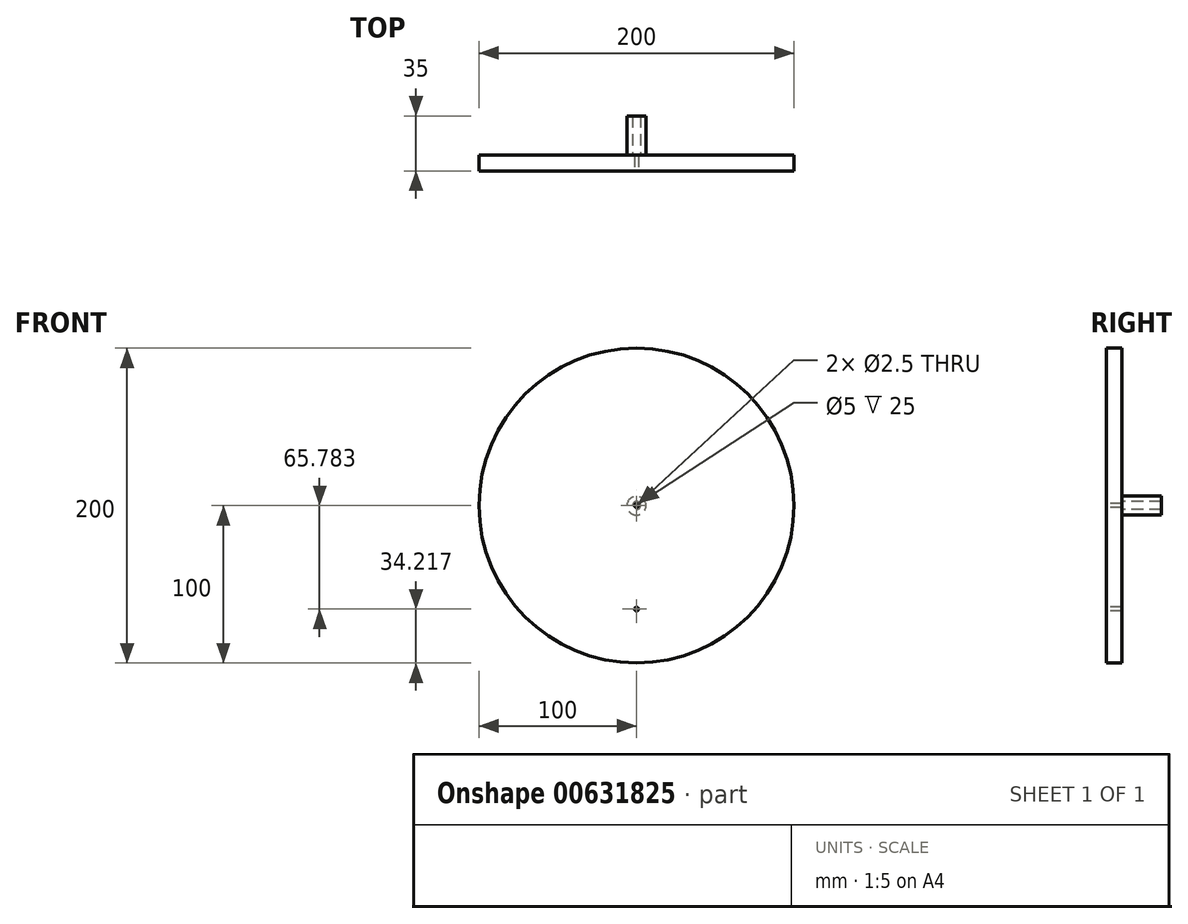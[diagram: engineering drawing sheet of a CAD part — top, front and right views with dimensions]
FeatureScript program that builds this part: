
annotation { "Feature Type Name" : "Feature", "Feature Type Description" : "" }
export const myFeature = defineFeature(function(context is Context, id is Id, definition is map)
    precondition{}
    {
        {
            var Q0;
            Q0=qCreatedBy(makeId("Front.planeOp"),FACE);
            var sketch = newSketch(context, id + "F0", { "sketchPlane" : qUnion([Q0])});
            skCircle(sketch, "E0", {"center": v(0, 0) * mm, "radius": 100 * mm});
            skSolve(sketch);
        }
        {
            var Q0;
            Q0 = qSketchRegion(id + "F0", true);
            extrude(context, id + "F1", {"entities" : qUnion([Q0]), "depth" : 10 * mm, "offsetDistance" : 25 * mm});
        }
        {
            var Q0;
            Q0=makeQuery(id+"F1.opExtrude","CAP_FACE",FACE,{"disambiguationData":[OSD([sQuery(id+"F0.wireOp",EDGE,"E0")])],"isStart":false});
            var sketch = newSketch(context, id + "F2", { "sketchPlane" : qUnion([Q0])});
            skPoint(sketch, "E1", {"position": v(0, 0) * mm});
            skPoint(sketch, "E2", {"position": v(0, -65.78) * mm});
            skSolve(sketch);
        }
        {
            var Q0;
            Q0=makeQuery(id+"F1.opExtrude","CAP_FACE",FACE,{"disambiguationData":[OSD([sQuery(id+"F0.wireOp",EDGE,"E0")])],"isStart":true});
            var sketch = newSketch(context, id + "F3", { "sketchPlane" : qUnion([Q0])});
            skCircle(sketch, "E3", {"center": v(0, 0) * mm, "radius": 6 * mm});
            skCircle(sketch, "E4", {"center": v(0, 0) * mm, "radius": 2.5 * mm});
            skSolve(sketch);
        }
        {
            var Q0;
            Q0=makeQuery(id+"F3.imprint","IMPRINT",FACE,{"disambiguationData":[TD([[makeQuery(id+"F3.imprint","IMPRINT",EDGE,{"derivedFrom":sQuery(id+"F3.wireOp",EDGE,"E3")}),1.0]])]});
            extrude(context, id + "F4", {"entities" : qUnion([Q0]), "operationType" : NewBodyOperationType.ADD, "depth" : 25 * mm, "offsetDistance" : 25 * mm});
        }
        {
            var Q0;
            Q0=sQuery(id+"F2.wireOp",VERTEX,"E1");
            var Q1;
            Q1=sQuery(id+"F2.wireOp",VERTEX,"E2");
            var Q2;
            Q2=makeQuery(id+"F1.opExtrude","SWEPT_BODY",BODY,{"disambiguationData":[OSD([sQuery(id+"F0.wireOp",EDGE,"E0")])]});
            hole(context, id + "F5", {"style" : HoleStyle.SIMPLE, "endStyle" : HoleEndStyle.THROUGH, "holeDiameter" : 2.5 * mm, "majorDiameter" : 5 * mm, "isTappedThrough" : true, "tappedDepth" : 12 * mm, "tapClearance" : 3, "locations" : qUnion([Q0, Q1]), "scope" : qUnion([Q2])});
        }
    });
